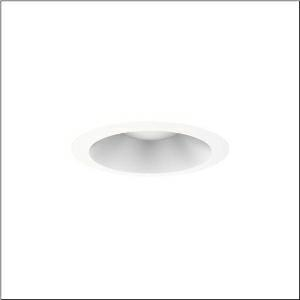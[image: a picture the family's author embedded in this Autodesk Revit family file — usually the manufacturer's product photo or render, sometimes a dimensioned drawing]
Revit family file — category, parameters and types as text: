
# Revit family: lunis_31-xl_51dn15mg42b
name_source: partatom
category: Lighting Fixtures
units: mm (PartAtom-declared; Revit-internal decimal feet)

## family parameters
Cut with Voids When Loaded = No
Host = Face
Light Source = No
Part Type = Normal
Room Calculation Point = No
Round Connector Dimension = Use Diameter
Shared = No

## types (1)
- --- (1 x LED, 2500 lm, 17 W, 4000K)
    Apparent Load = 17 VA
    CIE Flux Codes = 89 99 100 100 100
    Color Rendering = 80
    Color Temperature = 4000K
    Default Elevation = 1800 mm
    Description = Lunis 31-XL, downlight, light control with lens, light emission: direct distribution, LED rated luminous flux: 2.500lm, light colour: 840, mains connection: 220..240V, AC/DC, 0/50..60Hz, housing, of aluminium, white, protection rating (complete): IP20, protection rating (on room side): IP54, insulation class (complete): insulation class II (safety insulation), certification: CE, ENEC, packaging unit: 1 piece
    Height = 0 mm  [stored 0 ft]
    Lamp = 1 x LED
    Lamp Light Flux = 2500 lm
    Lamp Power = 17 W
    Lamp count = 1
    Length = 259 mm
    Luminous efficacy = 147 lm/W
    Manufacturer = Siteco
    ModVariant = No
    Model = 51DN15MG42B
    Mounting Place = Ceiling
    Mounting Type = Recessed
    Number of Poles = 1
    OnlyDefault = Yes
    Power Factor = 1
    Product Name = Lunis 31-XL
    Product group = downlight
    ProductGroupID = 401
    Protection Class = Protection class II
    Protection Degree = IP 20
    RLX_Detail_Level = 1
    RLX_Emergency_Light_Flux = 0 lm
    RLX_Emergency_Type = 0
    RLX_Emergency_Type_DB = No
    RlxData = <blob elided: 24269 chars, md5=66014957>
    Socket = socket
    Standby Power = 0 W
    System Light Flux = 2500 lm
    System Power = 17 W
    Type Comments = individual setting: luminous flux: 100 % | (ON | ON | ON | OFF) | 450 mA
    Type Image = l_1345915.jpg
    URL = http://relux.com
    VarID = @adj_029619
    Voltage = 0 V
    Weight = 0.00 kg
    Width = 0 mm  [stored 0 ft]

note: [stored X ft] marks values corroborated as IEEE doubles in the binary element streams (Revit-internal decimal feet)

## geometry (parser evidence)
native form markers: Blend x4, Sweep x10
no freeform markers — native parametric forms only
